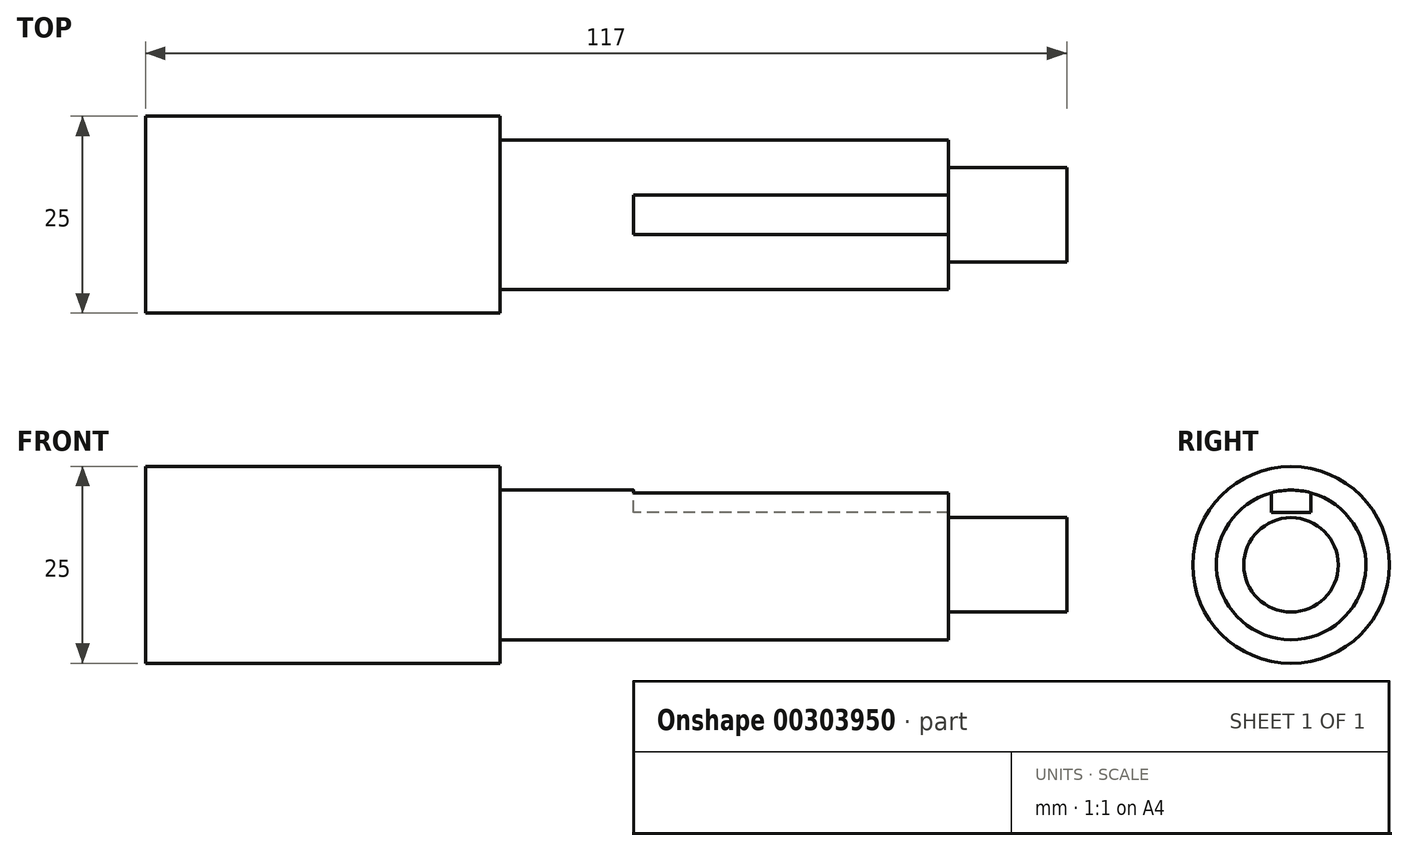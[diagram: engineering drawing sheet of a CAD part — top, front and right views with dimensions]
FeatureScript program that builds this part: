
annotation { "Feature Type Name" : "Feature", "Feature Type Description" : "" }
export const myFeature = defineFeature(function(context is Context, id is Id, definition is map)
    precondition{}
    {
        {
            var Q0;
            Q0=qCreatedBy(makeId("Right.planeOp"),FACE);
            var sketch = newSketch(context, id + "F0", { "sketchPlane" : qUnion([Q0])});
            skCircle(sketch, "E0", {"center": v(0, 0) * mm, "radius": 12.5 * mm});
            skSolve(sketch);
        }
        {
            var Q0;
            Q0=makeQuery(id+"F0.imprint","IMPRINT",FACE,{"disambiguationData":[TD([[makeQuery(id+"F0.imprint","IMPRINT",EDGE,{"derivedFrom":sQuery(id+"F0.wireOp",EDGE,"E0")}),1.0]])]});
            extrude(context, id + "F1", {"entities" : qUnion([Q0]), "depth" : 45 * mm});
        }
        {
            var Q0;
            Q0=makeQuery(id+"F1.opExtrude","CAP_FACE",FACE,{"disambiguationData":[OSD([sQuery(id+"F0.wireOp",EDGE,"E0")])],"isStart":false});
            var sketch = newSketch(context, id + "F2", { "sketchPlane" : qUnion([Q0])});
            skCircle(sketch, "E1", {"center": v(0, 0) * mm, "radius": 9.5 * mm});
            skPoint(sketch, "E2.middle", {"position": v(0, 9.5) * mm});
            skSolve(sketch);
        }
        {
            var Q0;
            Q0 = qSketchRegion(id + "F2", true);
            var Q1;
            Q1=sQuery(id+"F2.wireOp",EDGE,"E1");
            extrude(context, id + "F3", {"entities" : qUnion([Q0]), "surfaceEntities" : qUnion([Q1]), "depth" : 57 * mm});
        }
        {
            var Q0;
            Q0=makeQuery(id+"F3.opExtrude","CAP_FACE",FACE,{"disambiguationData":[OSD([sQuery(id+"F2.wireOp",EDGE,"E1")])],"isStart":false});
            var sketch = newSketch(context, id + "F4", { "sketchPlane" : qUnion([Q0])});
            skCircle(sketch, "E3", {"center": v(0, 0) * mm, "radius": 6 * mm});
            skLineSegment(sketch, "E4", {"start": v(-2.5, 6.67) * mm, "end": v(2.5, 6.67) * mm});
            skLineSegment(sketch, "E5", {"start": v(-2.5, 6.67) * mm, "end": v(-2.5, 9.17) * mm});
            skLineSegment(sketch, "E6", {"start": v(2.5, 6.67) * mm, "end": v(2.5, 9.17) * mm});
            skLineSegment(sketch, "E7", {"start": v(0, 9.5) * mm, "end": v(0, 6.67) * mm});
            skSolve(sketch);
        }
        {
            var Q0;
            Q0 = qSketchRegion(id + "F4", true);
            extrude(context, id + "F5", {"entities" : qUnion([Q0]), "operationType" : NewBodyOperationType.ADD, "depth" : 15 * mm});
        }
        {
            var Q0;
            {var subQ0=sQuery(id+"F4.wireOp",EDGE,"E6");Q0=makeQuery(id+"F4.imprint","IMPRINT",FACE,{"disambiguationData":[TD([[makeQuery(id+"F4.imprint","IMPRINT",EDGE,{"derivedFrom":subQ0}),1.0]])]});}
            var Q1;
            {var subQ0=sQuery(id+"F4.wireOp",EDGE,"E5");Q1=makeQuery(id+"F4.imprint","IMPRINT",FACE,{"disambiguationData":[TD([[makeQuery(id+"F4.imprint","IMPRINT",EDGE,{"derivedFrom":subQ0}),-1.0]])]});}
            extrude(context, id + "F6", {"entities" : qUnion([Q0, Q1]), "operationType" : NewBodyOperationType.REMOVE, "depth" : 80 * mm, "symmetric" : true});
        }
    });
